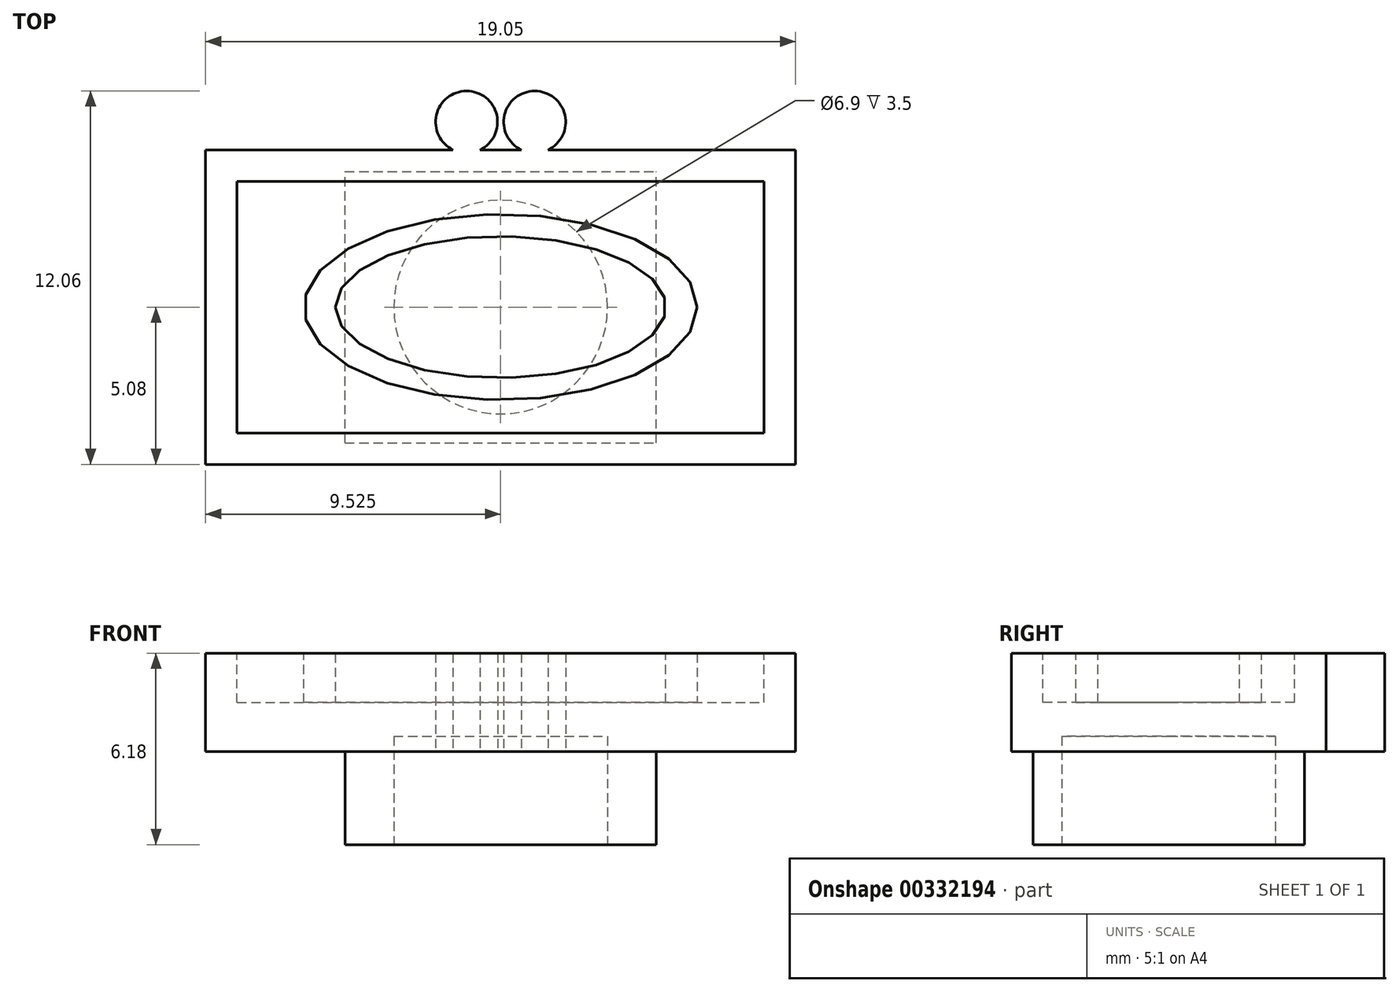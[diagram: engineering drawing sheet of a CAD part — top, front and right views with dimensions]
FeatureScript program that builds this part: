
annotation { "Feature Type Name" : "Feature", "Feature Type Description" : "" }
export const myFeature = defineFeature(function(context is Context, id is Id, definition is map)
    precondition{}
    {
        {
            var Q0;
            Q0=qCreatedBy(makeId("Top.planeOp"),FACE);
            var sketch = newSketch(context, id + "F0", { "sketchPlane" : qUnion([Q0])});
            skLineSegment(sketch, "E0.bottom", {"start": v(-19.05, 10.16) * mm, "end": v(0, 10.16) * mm});
            skLineSegment(sketch, "E0.top", {"start": v(-19.05, 0) * mm, "end": v(0, 0) * mm});
            skLineSegment(sketch, "E0.left", {"start": v(-19.05, 10.16) * mm, "end": v(-19.05, 0) * mm});
            skLineSegment(sketch, "E0.right", {"start": v(0, 10.16) * mm, "end": v(0, 0) * mm});
            skLineSegment(sketch, "E1", {"start": v(-9.52, 10.16) * mm, "end": v(-9.52, 0) * mm, "construction": true});
            skCircle(sketch, "E2", {"center": v(-10.62, 11.06) * mm, "radius": 1 * mm});
            skCircle(sketch, "E3.MirrorC", {"center": v(-8.42, 11.06) * mm, "radius": 1 * mm});
            skSolve(sketch);
        }
        {
            var Q0;
            Q0=qSketchRegion(id+"F0",true);
            extrude(context, id + "F1", {"entities" : qUnion([Q0]), "depth" : 3.17 * mm});
        }
        {
            var Q0;
            Q0=makeQuery(id+"F1.opExtrude","CAP_FACE",FACE,{"disambiguationData":[OSD([sQuery(id+"F0.wireOp",EDGE,"E0.bottom"),sQuery(id+"F0.wireOp",EDGE,"E0.top"),sQuery(id+"F0.wireOp",EDGE,"E0.left"),sQuery(id+"F0.wireOp",EDGE,"E0.right")])],"isStart":false});
            var sketch = newSketch(context, id + "F2", { "sketchPlane" : qUnion([Q0])});
            skLineSegment(sketch, "E4.bottom", {"start": v(-18.03, 9.14) * mm, "end": v(-1.02, 9.14) * mm});
            skLineSegment(sketch, "E4.top", {"start": v(-18.03, 1.02) * mm, "end": v(-1.02, 1.02) * mm});
            skLineSegment(sketch, "E4.left", {"start": v(-18.03, 9.14) * mm, "end": v(-18.03, 1.02) * mm});
            skLineSegment(sketch, "E4.right", {"start": v(-1.02, 9.14) * mm, "end": v(-1.02, 1.02) * mm});
            skSolve(sketch);
        }
        {
            var Q0;
            Q0=qSketchRegion(id+"F2",true);
            extrude(context, id + "F3", {"entities" : qUnion([Q0]), "operationType" : NewBodyOperationType.REMOVE, "oppositeDirection" : true, "depth" : 1.59 * mm});
        }
        {
            var Q0;
            {var subQ0=sQuery(id+"F2.wireOp",EDGE,"E4.bottom");var subQ1=sQuery(id+"F2.wireOp",EDGE,"E4.left");Q0=makeQuery(id+"FD6hazfNaiJcgqe_1.boolean.opBoolean","SPLIT",FACE,{"disambiguationData":[TD([makeQuery(id+"F3.boolean.opBoolean","COPY",FACE,{"derivedFrom":makeQuery(id+"F3.opExtrude","SWEPT_FACE",FACE,{"disambiguationData":[OSD([subQ0])]})})])],"derivedFrom":makeQuery(id+"F3.boolean.opBoolean","COPY",FACE,{"derivedFrom":makeQuery(id+"F3.opExtrude","CAP_FACE",FACE,{"disambiguationData":[OSD([subQ0,sQuery(id+"F2.wireOp",EDGE,"E4.top"),subQ1,sQuery(id+"F2.wireOp",EDGE,"E4.right")])],"isStart":false})})});}
            var sketch = newSketch(context, id + "F4", { "sketchPlane" : qUnion([Q0])});
            skLineSegment(sketch, "E5", {"start": v(-9.52, 10.16) * mm, "end": v(-9.52, 0) * mm, "construction": true});
            skLineSegment(sketch, "E6", {"start": v(-19.05, 5.08) * mm, "end": v(0, 5.08) * mm, "construction": true});
            skEllipse(sketch, "E7", {"center": v(-9.52, 5.08) * mm, "majorRadius": 5.33 * mm, "minorRadius": 2.29 * mm, "majorAxis": v(-1, 0)});
            skEllipse(sketch, "E8", {"center": v(-9.52, 5.08) * mm, "majorRadius": 6.35 * mm, "minorRadius": 3 * mm, "majorAxis": v(1, 0)});
            skSolve(sketch);
        }
        {
            var Q0;
            Q0=qSketchRegion(id+"F4",true);
            var Q1;
            Q1=makeQuery(id+"FD6hazfNaiJcgqe_1.boolean.opBoolean","MERGE",FACE,{"derivedFrom":[makeQuery(id+"F1.opExtrude","CAP_FACE",FACE,{"disambiguationData":[OSD([sQuery(id+"F0.wireOp",EDGE,"E0.bottom"),sQuery(id+"F0.wireOp",EDGE,"E0.top"),sQuery(id+"F0.wireOp",EDGE,"E0.left"),sQuery(id+"F0.wireOp",EDGE,"E0.right"),sQuery(id+"F0.wireOp",EDGE,"XctMcTzM-jzK6-gSmv-2nxO-Hmrl2WoydrkH.bottom"),sQuery(id+"F0.wireOp",EDGE,"XctMcTzM-jzK6-gSmv-2nxO-Hmrl2WoydrkH.left"),sQuery(id+"F0.wireOp",EDGE,"XctMcTzM-jzK6-gSmv-2nxO-Hmrl2WoydrkH.right")])],"isStart":false}),makeQuery(id+"FD6hazfNaiJcgqe_1.opExtrude","CAP_FACE",FACE,{"disambiguationData":[OSD([sQuery(id+"FBnKpMS2cNLFyNX_1.wireOp",EDGE,"OeS0QawB-iup7-bIXq-nBgO-fnigf9KOmNtt"),sQuery(id+"FBnKpMS2cNLFyNX_1.wireOp",EDGE,"xYslIAmR-IU4A-U8Ev-eRzx-1tLUXoU8zJ8x"),sQuery(id+"FBnKpMS2cNLFyNX_1.wireOp",EDGE,"s2yYm8nE-9nAX-yXiD-gElo-VwSO6LMNS3os"),sQuery(id+"FBnKpMS2cNLFyNX_1.wireOp",EDGE,"BWi2MzMB-bow1-vDxn-7ShQ-1YiDBgTSlN10"),sQuery(id+"FBnKpMS2cNLFyNX_1.wireOp",EDGE,"4fcJUz5v-7g5D-GTkM-eBk7-cmIldQICNH6a"),sQuery(id+"FBnKpMS2cNLFyNX_1.wireOp",EDGE,"JyWkrWma-j76y-q2y8-kGDN-Km0VDhZBhLyh"),sQuery(id+"FBnKpMS2cNLFyNX_1.wireOp",EDGE,"hH4EWFfC-tNwj-oGm0-8eoL-p1ctc8BhzRw8"),sQuery(id+"FBnKpMS2cNLFyNX_1.wireOp",EDGE,"unhDRoPr-LBfY-NyqK-AVhX-2gFjzCdnZd3x"),sQuery(id+"FBnKpMS2cNLFyNX_1.wireOp",EDGE,"eioCPEry-a7AL-AyuY-AUbQ-wWZvTsCijl4n"),sQuery(id+"FBnKpMS2cNLFyNX_1.wireOp",EDGE,"ga3sPcsW-uslI-afVP-5EuA-U3aNN3MUd2xP"),sQuery(id+"FBnKpMS2cNLFyNX_1.wireOp",EDGE,"2eZ3HgfS-F6HE-pDFD-BtrP-3SBC7ZAuQREh"),sQuery(id+"FBnKpMS2cNLFyNX_1.wireOp",EDGE,"egwDE0gL-gJxL-a5VO-DP01-p7e11LL6TNIh"),sQuery(id+"FBnKpMS2cNLFyNX_1.wireOp",EDGE,"Oc6yrfE5-Wmlw-YOVM-BoAX-kQYr9RLupFyV"),sQuery(id+"FBnKpMS2cNLFyNX_1.wireOp",EDGE,"HKjVjBGv-TE9a-NIGQ-HE8n-yFD3IG2zp62e")])],"isStart":false})]});
            extrude(context, id + "F5", {"entities" : qUnion([Q0]), "operationType" : NewBodyOperationType.ADD, "endBound" : BoundingType.UP_TO_SURFACE, "endBoundEntityFace" : qUnion([Q1]), "depth" : 25.4 * mm});
        }
        {
            var Q0;
            Q0=makeQuery(id+"F1.opExtrude","CAP_FACE",FACE,{"disambiguationData":[OSD([sQuery(id+"F0.wireOp",EDGE,"E0.bottom"),sQuery(id+"F0.wireOp",EDGE,"E0.top"),sQuery(id+"F0.wireOp",EDGE,"E0.left"),sQuery(id+"F0.wireOp",EDGE,"E0.right"),sQuery(id+"F0.wireOp",EDGE,"iD4YVwzi-38ZZ-sZow-cuPB-LK5aPxXRs2tg"),sQuery(id+"F0.wireOp",EDGE,"E2"),sQuery(id+"F0.wireOp",EDGE,"E3.MirrorC")])],"isStart":true});
            var sketch = newSketch(context, id + "F6", { "sketchPlane" : qUnion([Q0])});
            skLineSegment(sketch, "E9.bottom", {"start": v(-14.55, -0.7) * mm, "end": v(-4.5, -0.7) * mm});
            skLineSegment(sketch, "E9.top", {"start": v(-14.55, -9.46) * mm, "end": v(-4.5, -9.46) * mm});
            skLineSegment(sketch, "E9.left", {"start": v(-14.55, -0.7) * mm, "end": v(-14.55, -9.46) * mm});
            skLineSegment(sketch, "E9.right", {"start": v(-4.5, -0.7) * mm, "end": v(-4.5, -9.46) * mm});
            skSolve(sketch);
        }
        {
            var Q0;
            Q0=qSketchRegion(id+"F6",true);
            extrude(context, id + "F7", {"entities" : qUnion([Q0]), "operationType" : NewBodyOperationType.ADD, "depth" : 3 * mm, "offsetDistance" : 25 * mm});
        }
        {
            var Q0;
            Q0=makeQuery(id+"F7.opExtrude","CAP_FACE",FACE,{"disambiguationData":[OSD([sQuery(id+"F6.wireOp",EDGE,"E9.bottom"),sQuery(id+"F6.wireOp",EDGE,"E9.top"),sQuery(id+"F6.wireOp",EDGE,"E9.left"),sQuery(id+"F6.wireOp",EDGE,"E9.right")])],"isStart":false});
            var sketch = newSketch(context, id + "F8", { "sketchPlane" : qUnion([Q0])});
            skCircle(sketch, "E10", {"center": v(-9.52, -5.08) * mm, "radius": 3.45 * mm});
            skLineSegment(sketch, "E11", {"start": v(-19.05, -5.08) * mm, "end": v(0, -5.08) * mm, "construction": true});
            skPoint(sketch, "E11.endSnap0", {"position": v(-4.5, -5.08) * mm});
            skLineSegment(sketch, "E12", {"start": v(-9.53, 0) * mm, "end": v(-9.53, -9.46) * mm, "construction": true});
            skSolve(sketch);
        }
        {
            var Q0;
            Q0=makeQuery(id+"F8.imprint","IMPRINT",FACE,{"disambiguationData":[TD([[makeQuery(id+"F8.imprint","IMPRINT",EDGE,{"derivedFrom":sQuery(id+"F8.wireOp",EDGE,"E10")}),1.0]])]});
            extrude(context, id + "F9", {"entities" : qUnion([Q0]), "operationType" : NewBodyOperationType.REMOVE, "oppositeDirection" : true, "depth" : 3.5 * mm, "offsetDistance" : 25 * mm});
        }
    });
